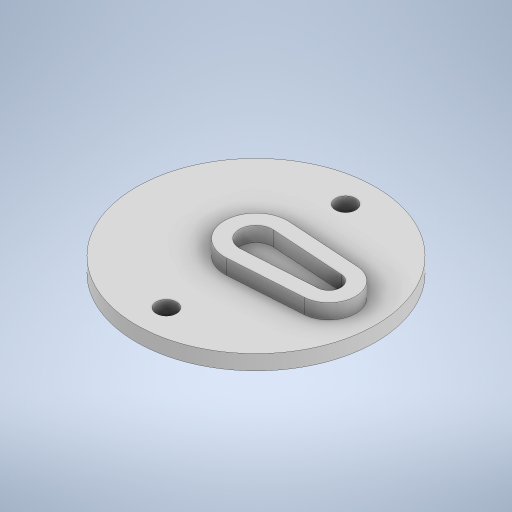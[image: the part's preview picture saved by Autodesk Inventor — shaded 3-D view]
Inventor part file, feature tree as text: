
AUTODESK INVENTOR PART (.ipt)
format: ipt  version: 2024 (Build 280153000, 153)  size: 258,048 bytes
history: native  units: in
note: dims shown in document units (in); Inventor stores cm internally (conversion verified against a paired STEP export)
features: extrude x2, sketch x2
ambient origin geometry x8: Origin, YZ Plane, XZ Plane, XY Plane, X Axis, Y Axis, Z Axis, Center Point
bodies: Solid1 (feature_tree)
feature tree (4):
  extrude  "Extrusion1"  Depth=0.17in
  extrude  "Extrusion2"  Depth=0.125in
  sketch  "Sketch1"  dims[d0=2.0in d1=0.17in]
  sketch  "Sketch2"  dims[d2=0.17in d3=1.5in d4=0.125in d5=0.0in d6=0.2756in d7=0.1969in d8=0.8465in d9=0.125in d10=0.125in d11=0.0in]
